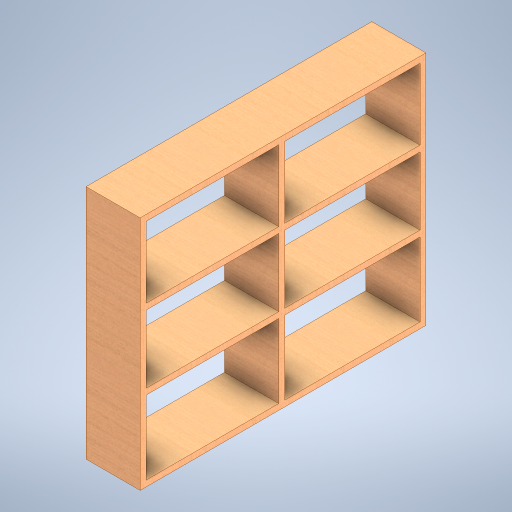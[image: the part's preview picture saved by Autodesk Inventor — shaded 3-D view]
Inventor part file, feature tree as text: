
AUTODESK INVENTOR PART (.ipt)
format: ipt  version: 2023 (Build 270158000, 158)  size: 454,656 bytes
history: native  units: in
note: dims shown in document units (in); Inventor stores cm internally (conversion verified against a paired STEP export)
features: extrude x1, sketch x1
ambient origin geometry x8: Origin, YZ Plane, XZ Plane, XY Plane, X Axis, Y Axis, Z Axis, Center Point
bodies: Solid1 (feature_tree)
feature tree (2):
  extrude  "Extrusion1"  Depth=0.4331in
  sketch  "Sketch1"  dims[d9=0.4331in d10=0.4331in d11=0.4331in d12=0.4331in d13=0.4331in d14=16.2992in d15=19.9213in d16=9.8425in d17=0.4331in d18=5.1575in d19=0.4331in d20=5.3543in d21=4.9213in d22=3.937in d23=0.0in]
